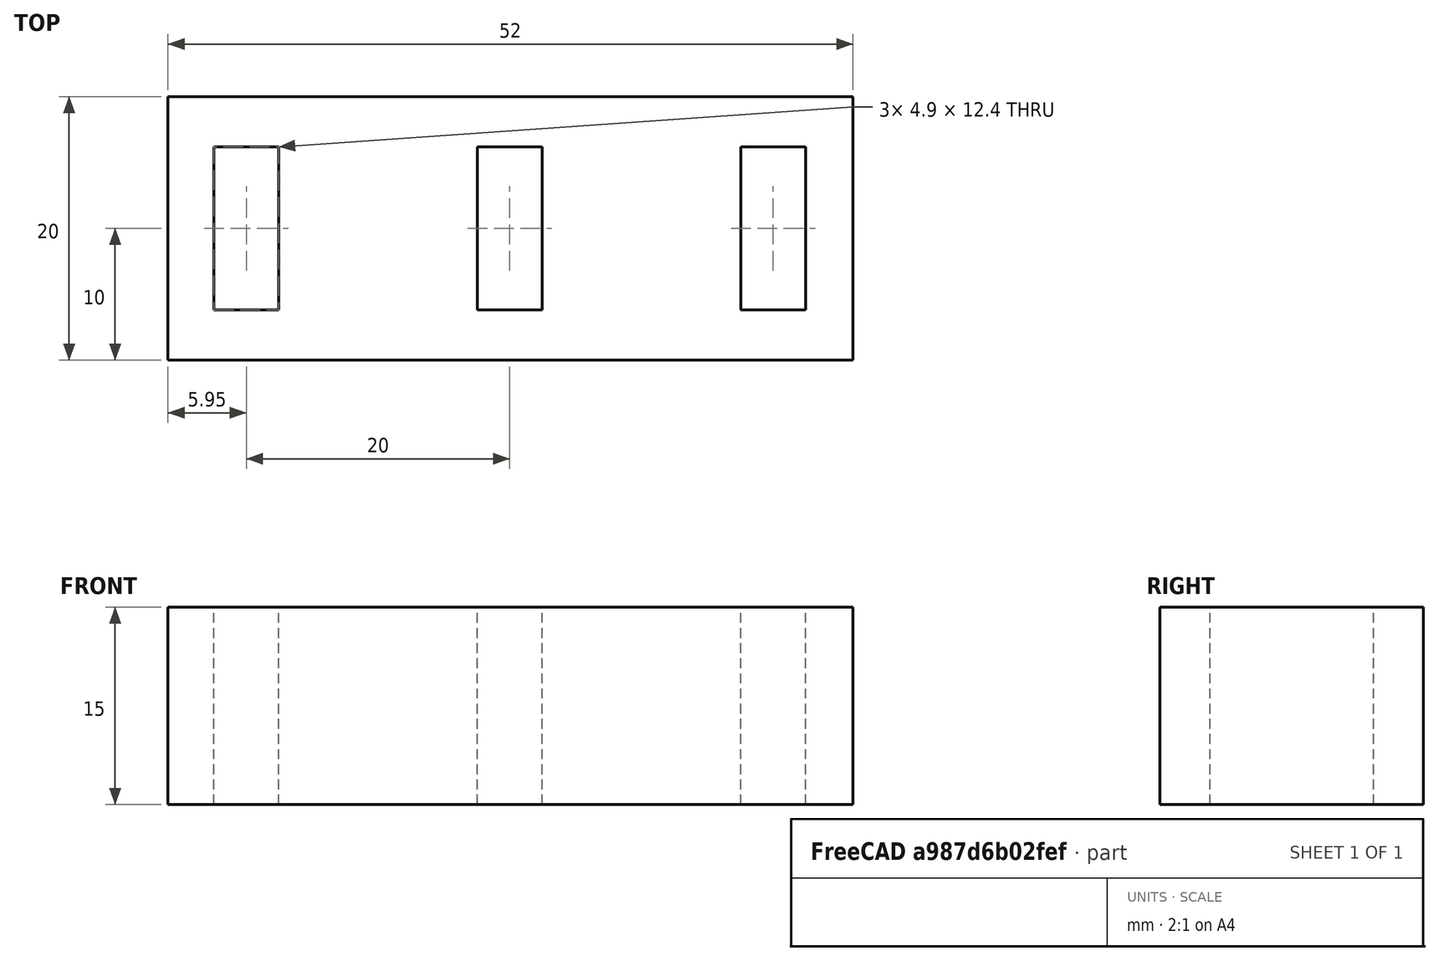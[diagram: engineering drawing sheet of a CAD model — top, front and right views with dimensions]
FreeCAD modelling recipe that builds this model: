
FCSTD DOCUMENT  (FreeCAD 0.19R24291 (Git))
Label: reto4
License: All rights reserved
LicenseURL: http://en.wikipedia.org/wiki/All_rights_reserved
objects: App::MeasureDistance×6, Part::Box×4, Part::MultiFuse×1, Part::Cut×1
note: 6 computed .brp shape members not serialized (recipe doc carries the construction recipe); baked Part::Feature solids carry a one-line shape summary decoded from their .brp

FEATURE [Part::Box] Box  label="Cube"
  AttacherType = Attacher::AttachEngine3D
  Height = 15
  Length = 52
  Width = 20
FEATURE [Part::Box] Box001  label="Cube001"
  AttacherType = Attacher::AttachEngine3D
  Height = 25
  Length = 4.9
  Placement = pos=(3.5,3.8,-2) rot=(0,0,1;0rad)
  Width = 12.4
FEATURE [Part::Box] Box002  label="Cube002"
  AttacherType = Attacher::AttachEngine3D
  Height = 25
  Length = 4.9
  Placement = pos=(23.5,3.8,-2) rot=(0,0,1;0rad)
  Width = 12.4
FEATURE [Part::Box] Box003  label="Cube003"
  AttacherType = Attacher::AttachEngine3D
  Height = 25
  Length = 4.9
  Placement = pos=(43.5,3.8,-2) rot=(0,0,1;0rad)
  Width = 12.4
FEATURE [Part::MultiFuse] Fusion
  Refine = true
  Shapes = -> [Box001,Box002,Box003]
FEATURE [Part::Cut] Cut
  Base = -> Box
  Refine = true
  Tool = -> Fusion
FEATURE [App::MeasureDistance] Distance  label="Distance: 51,98 mm"
  Distance = 51.9751
  P1 = (52,20,15)
  P2 = (0.0248536,19.982,15)
FEATURE [App::MeasureDistance] Distance001  label="Distance: 14,99 mm"
  Distance = 14.9933
  P1 = (52,20,15)
  P2 = (52,19.9535,0.00681569)
FEATURE [App::MeasureDistance] Distance002  label="Distance: 19,95 mm"
  Distance = 19.9477
  P1 = (52,0,0)
  P2 = (52,19.9477,0)
FEATURE [App::MeasureDistance] Distance003  label="Distance: 4,90 mm"
  Distance = 4.90098
  P1 = (28.421,3.7977,15)
  P2 = (23.52,3.8,15)
FEATURE [App::MeasureDistance] Distance004  label="Distance: 12,39 mm"
  Distance = 12.3948
  P1 = (8.4,3.8,15)
  P2 = (8.4,16.1948,15)
FEATURE [App::MeasureDistance] Distance005  label="Distance: 19,98 mm"
  Distance = 19.9781
  P1 = (28.4219,16.1877,15)
  P2 = (48.4,16.1888,15)
